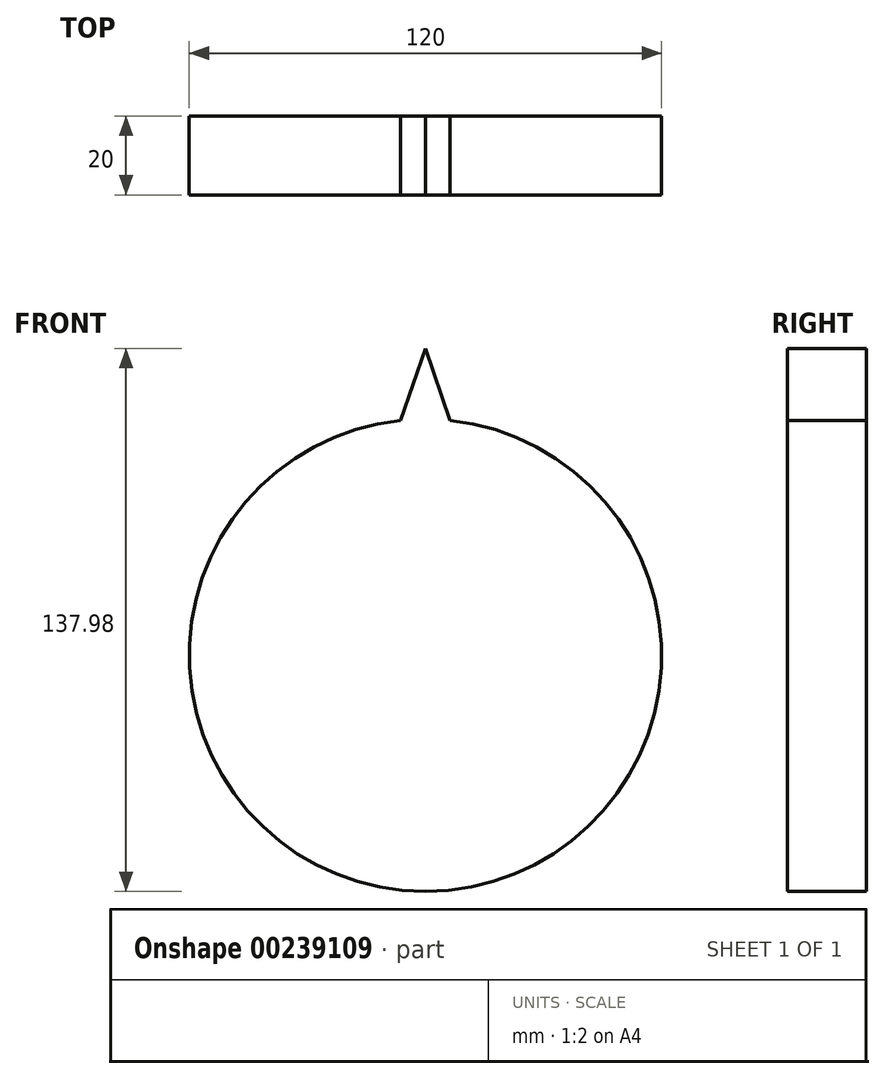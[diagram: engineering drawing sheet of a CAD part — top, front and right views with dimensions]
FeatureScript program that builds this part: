
annotation { "Feature Type Name" : "Feature", "Feature Type Description" : "" }
export const myFeature = defineFeature(function(context is Context, id is Id, definition is map)
    precondition{}
    {
        {
            var Q0;
            Q0=qCreatedBy(makeId("Front.planeOp"),FACE);
            var sketch = newSketch(context, id + "F0", { "sketchPlane" : qUnion([Q0])});
            skCircle(sketch, "E0", {"center": v(0, 0) * mm, "radius": 60 * mm});
            skSolve(sketch);
        }
        {
            var Q0;
            Q0 = qSketchRegion(id + "F0", true);
            extrude(context, id + "F1", {"entities" : qUnion([Q0]), "depth" : 20 * mm});
        }
        {
            var Q0;
            Q0=makeQuery(id+"F1.opExtrude","CAP_FACE",FACE,{"disambiguationData":[OSD([sQuery(id+"F0.wireOp",EDGE,"E0")])],"isStart":false});
            var sketch = newSketch(context, id + "F2", { "sketchPlane" : qUnion([Q0])});
            skLineSegment(sketch, "E1", {"start": v(0, 0) * mm, "end": v(6.27, 59.67) * mm, "construction": true});
            skLineSegment(sketch, "E2", {"start": v(6.27, 59.67) * mm, "end": v(-6.27, 59.67) * mm, "construction": true});
            skLineSegment(sketch, "E3", {"start": v(-6.27, 59.67) * mm, "end": v(0, 0) * mm, "construction": true});
            skLineSegment(sketch, "E4", {"start": v(-6.27, 59.67) * mm, "end": v(0, 77.98) * mm});
            skLineSegment(sketch, "E5", {"start": v(0, 77.98) * mm, "end": v(6.27, 59.67) * mm});
            skLineSegment(sketch, "E6", {"start": v(-6.27, 59.67) * mm, "end": v(6.27, 59.67) * mm});
            skSolve(sketch);
        }
        {
            var Q0;
            Q0 = qSketchRegion(id + "F2", true);
            extrude(context, id + "F3", {"entities" : qUnion([Q0]), "operationType" : NewBodyOperationType.ADD, "oppositeDirection" : true, "depth" : 20 * mm});
        }
    });
